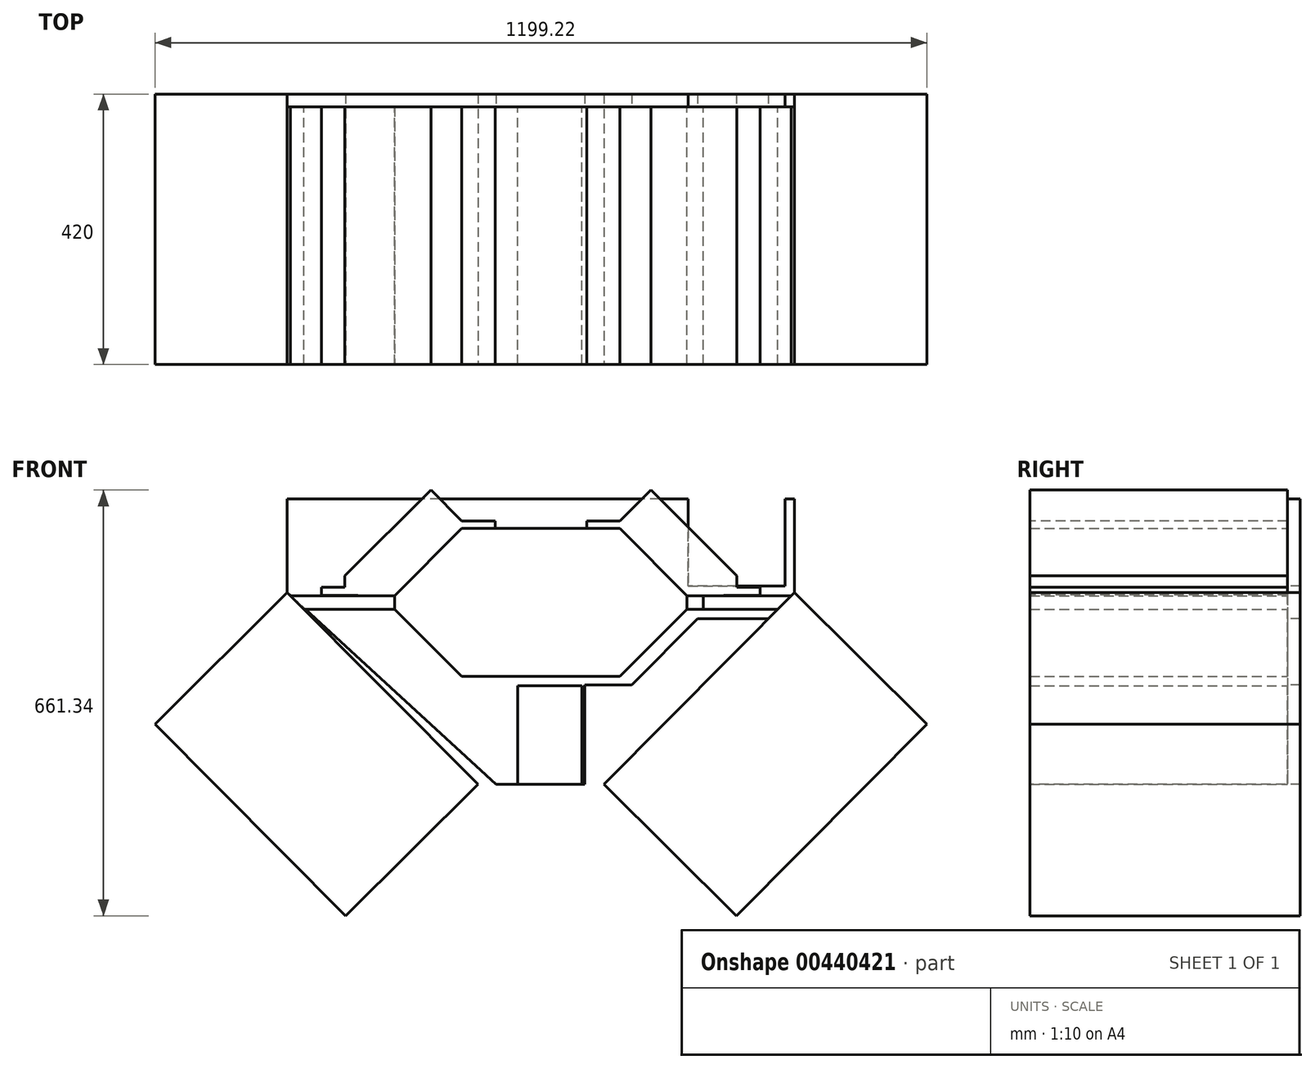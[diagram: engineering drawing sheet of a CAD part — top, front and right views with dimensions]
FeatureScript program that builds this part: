
annotation { "Feature Type Name" : "Feature", "Feature Type Description" : "" }
export const myFeature = defineFeature(function(context is Context, id is Id, definition is map)
    precondition{}
    {
        {
            var Q0;
            Q0=qCreatedBy(makeId("Front.planeOp"),FACE);
            var sketch = newSketch(context, id + "F0", { "sketchPlane" : qUnion([Q0])});
            skLineSegment(sketch, "E0", {"start": v(-123, -114.98) * mm, "end": v(-227.04, -10.5) * mm});
            skLineSegment(sketch, "E1", {"start": v(-227.04, -10.5) * mm, "end": v(-227.04, 10.5) * mm});
            skLineSegment(sketch, "E2", {"start": v(-227.04, 10.5) * mm, "end": v(-123.04, 115.02) * mm});
            skLineSegment(sketch, "E3", {"start": v(-123.04, 115.02) * mm, "end": v(122.96, 115.02) * mm});
            skLineSegment(sketch, "E4", {"start": v(122.96, 115.02) * mm, "end": v(226.96, 10.5) * mm});
            skLineSegment(sketch, "E5", {"start": v(226.96, 10.5) * mm, "end": v(226.96, -10.5) * mm});
            skLineSegment(sketch, "E6", {"start": v(226.96, -10.5) * mm, "end": v(123, -115.06) * mm});
            skLineSegment(sketch, "E7", {"start": v(123, -115.06) * mm, "end": v(-123, -114.98) * mm});
            skLineSegment(sketch, "E8", {"start": v(-106.88, 0) * mm, "end": v(-643.2, 0) * mm, "construction": true});
            skPoint(sketch, "E8.startSnap0", {"position": v(226.96, 0) * mm});
            skPoint(sketch, "E8.endSnap0", {"position": v(-227.04, 0) * mm});
            skPoint(sketch, "E9.endSnap0", {"position": v(0, -115.02) * mm});
            skLineSegment(sketch, "E10", {"start": v(0, -278.91) * mm, "end": v(0, 42.54) * mm, "construction": true});
            skPoint(sketch, "E11", {"position": v(0, 0) * mm});
            skSolve(sketch);
        }
        {
            var Q0;
            Q0=makeQuery(id+"F0.imprint","IMPRINT",FACE,{"disambiguationData":[TD([[makeQuery(id+"F0.imprint","IMPRINT",EDGE,{"derivedFrom":sQuery(id+"F0.wireOp",EDGE,"E0")}),-1.0]])]});
            extrude(context, id + "F1", {"entities" : qUnion([Q0]), "depth" : 400 * mm});
        }
        {
            var Q0;
            Q0=makeQuery(id+"F1.opExtrude","SWEPT_FACE",FACE,{"disambiguationData":[OSD([sQuery(id+"F0.wireOp",EDGE,"E5")])]});
            extrude(context, id + "F2", {"entities" : qUnion([Q0]), "depth" : 25 * mm});
        }
        {
            var Q0;
            Q0=makeQuery(id+"F1.opExtrude","CAP_FACE",FACE,{"disambiguationData":[OSD([sQuery(id+"F0.wireOp",EDGE,"E0"),sQuery(id+"F0.wireOp",EDGE,"E1"),sQuery(id+"F0.wireOp",EDGE,"E2"),sQuery(id+"F0.wireOp",EDGE,"E3"),sQuery(id+"F0.wireOp",EDGE,"E4"),sQuery(id+"F0.wireOp",EDGE,"E5"),sQuery(id+"F0.wireOp",EDGE,"E6"),sQuery(id+"F0.wireOp",EDGE,"E7")])],"isStart":false});
            var sketch = newSketch(context, id + "F3", { "sketchPlane" : qUnion([Q0])});
            skLineSegment(sketch, "E12.0", {"start": v(226.96, -10.5) * mm, "end": v(123, -115.06) * mm, "construction": true});
            skLineSegment(sketch, "E13.0", {"start": v(263.26, -115.82) * mm, "end": v(97.84, -282.21) * mm, "construction": true});
            skLineSegment(sketch, "E14.bottom", {"start": v(97.84, -282.21) * mm, "end": v(303.5, -486.67) * mm});
            skLineSegment(sketch, "E14.top", {"start": v(393.95, 15.64) * mm, "end": v(599.61, -188.82) * mm});
            skLineSegment(sketch, "E14.left", {"start": v(97.84, -282.21) * mm, "end": v(393.95, 15.64) * mm});
            skLineSegment(sketch, "E14.right", {"start": v(303.5, -486.67) * mm, "end": v(599.61, -188.82) * mm});
            skLineSegment(sketch, "E15", {"start": v(97.84, -282.21) * mm, "end": v(599.61, -188.82) * mm, "construction": true});
            skLineSegment(sketch, "E16", {"start": v(393.95, 15.64) * mm, "end": v(303.5, -486.67) * mm, "construction": true});
            skPoint(sketch, "E17", {"position": v(348.72, -235.52) * mm});
            skPoint(sketch, "E18", {"position": v(174.98, -62.78) * mm});
            skLineSegment(sketch, "E19", {"start": v(174.98, -62.78) * mm, "end": v(348.72, -235.52) * mm, "construction": true});
            skSolve(sketch);
        }
        {
            var Q0;
            Q0=makeQuery(id+"F3.imprint","IMPRINT",FACE,{"disambiguationData":[TD([[makeQuery(id+"F3.imprint","IMPRINT",EDGE,{"derivedFrom":sQuery(id+"F3.wireOp",EDGE,"E14.bottom")}),1.0]])]});
            extrude(context, id + "F4", {"entities" : qUnion([Q0]), "oppositeDirection" : true, "depth" : 420 * mm});
        }
        {
            var Q0;
            Q0=makeQuery(id+"F4.opExtrude","SWEPT_BODY",BODY,{"disambiguationData":[OSD([sQuery(id+"F3.wireOp",EDGE,"E14.bottom"),sQuery(id+"F3.wireOp",EDGE,"E14.top"),sQuery(id+"F3.wireOp",EDGE,"E14.left"),sQuery(id+"F3.wireOp",EDGE,"E14.right")])]});
            var Q1;
            Q1=qCreatedBy(makeId("Right.planeOp"),FACE);
            mirror(context, id + "F5", {"entities" : qUnion([Q0]), "mirrorPlane" : qUnion([Q1])});
        }
        {
            var Q0;
            Q0=makeQuery(id+"F2.opExtrude","CAP_FACE",FACE,{"disambiguationData":[OSD([sQuery(id+"F0.wireOp",EDGE,"E5")])],"isStart":false});
            extrude(context, id + "F6", {"entities" : qUnion([Q0]), "endBound" : BoundingType.UP_TO_NEXT, "depth" : 25 * mm});
        }
        {
            var Q0;
            Q0=makeQuery(id+"F1.opExtrude","SWEPT_FACE",FACE,{"disambiguationData":[OSD([sQuery(id+"F0.wireOp",EDGE,"E1")])]});
            extrude(context, id + "F7", {"entities" : qUnion([Q0]), "endBound" : BoundingType.UP_TO_NEXT, "depth" : 25 * mm});
        }
        {
            var Q0;
            Q0=makeQuery(id+"F1.opExtrude","CAP_FACE",FACE,{"disambiguationData":[OSD([sQuery(id+"F0.wireOp",EDGE,"E0"),sQuery(id+"F0.wireOp",EDGE,"E1"),sQuery(id+"F0.wireOp",EDGE,"E2"),sQuery(id+"F0.wireOp",EDGE,"E3"),sQuery(id+"F0.wireOp",EDGE,"E4"),sQuery(id+"F0.wireOp",EDGE,"E5"),sQuery(id+"F0.wireOp",EDGE,"E6"),sQuery(id+"F0.wireOp",EDGE,"E7")])],"isStart":false});
            var sketch = newSketch(context, id + "F8", { "sketchPlane" : qUnion([Q0])});
            skLineSegment(sketch, "E20", {"start": v(122.96, 115.02) * mm, "end": v(71.26, 115.02) * mm});
            skLineSegment(sketch, "E21", {"start": v(71.26, 115.02) * mm, "end": v(71.26, 126.66) * mm});
            skLineSegment(sketch, "E22", {"start": v(71.26, 126.66) * mm, "end": v(122.96, 126.66) * mm});
            skLineSegment(sketch, "E23", {"start": v(122.96, 126.66) * mm, "end": v(170.93, 174.67) * mm});
            skLineSegment(sketch, "E24", {"start": v(170.93, 174.67) * mm, "end": v(304.57, 41.13) * mm});
            skLineSegment(sketch, "E25", {"start": v(304.57, 41.13) * mm, "end": v(304.57, 23.86) * mm});
            skLineSegment(sketch, "E26", {"start": v(304.57, 23.86) * mm, "end": v(340.52, 23.86) * mm});
            skLineSegment(sketch, "E27", {"start": v(340.52, 23.86) * mm, "end": v(340.52, 11.86) * mm});
            skLineSegment(sketch, "E28", {"start": v(340.52, 11.86) * mm, "end": v(226.96, 10.5) * mm});
            skLineSegment(sketch, "E29", {"start": v(226.96, 10.5) * mm, "end": v(122.96, 115.02) * mm});
            skSolve(sketch);
        }
        {
            var Q0;
            Q0=makeQuery(id+"F8.imprint","IMPRINT",FACE,{"disambiguationData":[TD([[makeQuery(id+"F8.imprint","IMPRINT",EDGE,{"derivedFrom":sQuery(id+"F8.wireOp",EDGE,"E20")}),1.0]])]});
            extrude(context, id + "F9", {"entities" : qUnion([Q0]), "oppositeDirection" : true, "depth" : 400 * mm});
        }
        {
            var Q0;
            Q0=makeQuery(id+"F9.opExtrude","SWEPT_BODY",BODY,{"disambiguationData":[OSD([sQuery(id+"F8.wireOp",EDGE,"E20"),sQuery(id+"F8.wireOp",EDGE,"E21"),sQuery(id+"F8.wireOp",EDGE,"E22"),sQuery(id+"F8.wireOp",EDGE,"E23"),sQuery(id+"F8.wireOp",EDGE,"E24"),sQuery(id+"F8.wireOp",EDGE,"E25"),sQuery(id+"F8.wireOp",EDGE,"E26"),sQuery(id+"F8.wireOp",EDGE,"E27"),sQuery(id+"F8.wireOp",EDGE,"E28"),sQuery(id+"F8.wireOp",EDGE,"E29")])]});
            var Q1;
            Q1=qCreatedBy(makeId("Right.planeOp"),FACE);
            mirror(context, id + "F10", {"entities" : qUnion([Q0]), "mirrorPlane" : qUnion([Q1])});
        }
        {
            var Q0;
            Q0=makeQuery(id+"F1.opExtrude","CAP_FACE",FACE,{"disambiguationData":[OSD([sQuery(id+"F0.wireOp",EDGE,"E0"),sQuery(id+"F0.wireOp",EDGE,"E1"),sQuery(id+"F0.wireOp",EDGE,"E2"),sQuery(id+"F0.wireOp",EDGE,"E3"),sQuery(id+"F0.wireOp",EDGE,"E4"),sQuery(id+"F0.wireOp",EDGE,"E5"),sQuery(id+"F0.wireOp",EDGE,"E6"),sQuery(id+"F0.wireOp",EDGE,"E7")])],"isStart":true});
            var sketch = newSketch(context, id + "F11", { "sketchPlane" : qUnion([Q0])});
            skLineSegment(sketch, "E30", {"start": v(-226.96, -10.5) * mm, "end": v(-367.97, -10.5) * mm});
            skLineSegment(sketch, "E31", {"start": v(-367.97, -10.5) * mm, "end": v(-393.95, 15.64) * mm});
            skLineSegment(sketch, "E32", {"start": v(-393.95, 15.64) * mm, "end": v(-393.95, 160.92) * mm});
            skLineSegment(sketch, "E33", {"start": v(-393.95, 160.92) * mm, "end": v(-186.53, 160.92) * mm});
            skLineSegment(sketch, "E34", {"start": v(-186.53, 160.92) * mm, "end": v(156.41, 160.92) * mm});
            skLineSegment(sketch, "E35", {"start": v(156.41, 160.92) * mm, "end": v(393.95, 160.92) * mm});
            skLineSegment(sketch, "E36", {"start": v(393.95, 160.92) * mm, "end": v(393.95, 15.64) * mm});
            skLineSegment(sketch, "E37", {"start": v(393.95, 15.64) * mm, "end": v(69.96, -282.21) * mm});
            skLineSegment(sketch, "E38", {"start": v(69.96, -282.21) * mm, "end": v(-97.84, -282.21) * mm});
            skLineSegment(sketch, "E39", {"start": v(-97.84, -282.21) * mm, "end": v(-367.97, -10.5) * mm});
            skPoint(sketch, "E40.0", {"position": v(-393.95, 15.64) * mm});
            skPoint(sketch, "E41.0", {"position": v(-97.84, -282.21) * mm});
            skPoint(sketch, "E42.0", {"position": v(97.84, -282.21) * mm});
            skPoint(sketch, "E43.0", {"position": v(393.95, 15.64) * mm});
            skPoint(sketch, "E44.0", {"position": v(-367.97, -10.5) * mm});
            skSolve(sketch);
        }
        {
            var Q0;
            Q0=makeQuery(id+"F11.imprint","IMPRINT",FACE,{"disambiguationData":[TD([[makeQuery(id+"F11.imprint","IMPRINT",EDGE,{"derivedFrom":sQuery(id+"F11.wireOp",EDGE,"E31")}),-1.0]])]});
            var Q1;
            Q1=makeQuery(id+"F11.imprint","IMPRINT",FACE,{"disambiguationData":[TD([[makeQuery(id+"F11.imprint","IMPRINT",EDGE,{"derivedFrom":makeQuery(id+"F1.opExtrude","CAP_EDGE",EDGE,{"disambiguationData":[OSD([sQuery(id+"F0.wireOp",EDGE,"E0")])],"isStart":true})}),1.0]])]});
            extrude(context, id + "F12", {"entities" : qUnion([Q0, Q1]), "depth" : 20 * mm});
        }
        {
            var Q0;
            Q0=makeQuery(id+"F12.opExtrude","CAP_FACE",FACE,{"disambiguationData":[OSD([sQuery(id+"F11.wireOp",EDGE,"E31"),sQuery(id+"F11.wireOp",EDGE,"E32"),sQuery(id+"F11.wireOp",EDGE,"E33"),sQuery(id+"F11.wireOp",EDGE,"E34"),sQuery(id+"F11.wireOp",EDGE,"E35"),sQuery(id+"F11.wireOp",EDGE,"E36"),sQuery(id+"F11.wireOp",EDGE,"E37"),sQuery(id+"F11.wireOp",EDGE,"E38"),sQuery(id+"F11.wireOp",EDGE,"E39")])],"isStart":true});
            var sketch = newSketch(context, id + "F13", { "sketchPlane" : qUnion([Q0])});
            skLineSegment(sketch, "E45", {"start": v(353.05, -25.5) * mm, "end": v(243.07, -25.5) * mm});
            skLineSegment(sketch, "E46", {"start": v(243.07, -25.5) * mm, "end": v(140.84, -128.33) * mm});
            skLineSegment(sketch, "E47", {"start": v(67.84, -128.33) * mm, "end": v(67.84, -282.21) * mm});
            skLineSegment(sketch, "E48", {"start": v(67.84, -282.21) * mm, "end": v(97.84, -282.21) * mm});
            skLineSegment(sketch, "E49", {"start": v(97.84, -282.21) * mm, "end": v(353.05, -25.5) * mm});
            skLineSegment(sketch, "E50.bottom", {"start": v(378.95, 25.5) * mm, "end": v(228.95, 25.5) * mm});
            skLineSegment(sketch, "E50.top", {"start": v(378.95, 165.5) * mm, "end": v(228.95, 165.5) * mm});
            skLineSegment(sketch, "E50.left", {"start": v(378.95, 25.5) * mm, "end": v(378.95, 165.5) * mm});
            skLineSegment(sketch, "E50.right", {"start": v(228.95, 25.5) * mm, "end": v(228.95, 165.5) * mm});
            skLineSegment(sketch, "E51.MirrorCS", {"start": v(-228.95, 25.5) * mm, "end": v(-228.95, 165.5) * mm});
            skLineSegment(sketch, "E52.MirrorCS", {"start": v(-378.95, 165.5) * mm, "end": v(-228.95, 165.5) * mm});
            skLineSegment(sketch, "E53.MirrorCS", {"start": v(-378.95, 25.5) * mm, "end": v(-378.95, 165.5) * mm});
            skLineSegment(sketch, "E54.MirrorCS", {"start": v(-378.95, 25.5) * mm, "end": v(-228.95, 25.5) * mm});
            skLineSegment(sketch, "E55.MirrorCS", {"start": v(-353.05, -25.5) * mm, "end": v(-243.07, -25.5) * mm});
            skLineSegment(sketch, "E56.MirrorCS", {"start": v(-97.84, -282.21) * mm, "end": v(-353.05, -25.5) * mm});
            skLineSegment(sketch, "E57.MirrorCS", {"start": v(-67.84, -282.21) * mm, "end": v(-97.84, -282.21) * mm});
            skLineSegment(sketch, "E58", {"start": v(140.84, -128.33) * mm, "end": v(67.84, -128.33) * mm});
            skLineSegment(sketch, "E59.MirrorCS", {"start": v(-67.84, -128.33) * mm, "end": v(-67.84, -282.21) * mm});
            skLineSegment(sketch, "E60.MirrorCS", {"start": v(-140.84, -128.33) * mm, "end": v(-67.84, -128.33) * mm});
            skLineSegment(sketch, "E61.MirrorCS", {"start": v(-243.07, -25.5) * mm, "end": v(-140.84, -128.33) * mm});
            skLineSegment(sketch, "E62.bottom", {"start": v(13.94, -282.21) * mm, "end": v(-36.06, -282.21) * mm});
            skLineSegment(sketch, "E62.top", {"start": v(13.94, -129.54) * mm, "end": v(-36.06, -129.54) * mm});
            skLineSegment(sketch, "E62.left", {"start": v(13.94, -282.21) * mm, "end": v(13.94, -129.54) * mm, "construction": true});
            skLineSegment(sketch, "E62.right", {"start": v(-36.06, -282.21) * mm, "end": v(-36.06, -129.54) * mm});
            skLineSegment(sketch, "E63.MirrorCS", {"start": v(13.94, -129.54) * mm, "end": v(63.94, -129.54) * mm});
            skLineSegment(sketch, "E64.MirrorCS", {"start": v(63.94, -282.21) * mm, "end": v(63.94, -129.54) * mm});
            skLineSegment(sketch, "E65.MirrorCS", {"start": v(13.94, -282.21) * mm, "end": v(63.94, -282.21) * mm});
            skSolve(sketch);
        }
        {
            var Q0;
            Q0=makeQuery(id+"F13.imprint","IMPRINT",FACE,{"disambiguationData":[TD([[makeQuery(id+"F13.imprint","IMPRINT",EDGE,{"derivedFrom":sQuery(id+"F13.wireOp",EDGE,"E62.bottom")}),1.0]])]});
            extrude(context, id + "F14", {"entities" : qUnion([Q0]), "depth" : 400 * mm});
        }
        {
            var Q0;
            Q0=makeQuery(id+"F13.imprint","IMPRINT",FACE,{"disambiguationData":[TD([[makeQuery(id+"F13.imprint","IMPRINT",EDGE,{"derivedFrom":sQuery(id+"F13.wireOp",EDGE,"E55.MirrorCS")}),-1.0]])]});
            var Q1;
            Q1=makeQuery(id+"F13.imprint","IMPRINT",FACE,{"disambiguationData":[TD([[makeQuery(id+"F13.imprint","IMPRINT",EDGE,{"derivedFrom":sQuery(id+"F13.wireOp",EDGE,"E45")}),1.0]])]});
            var Q2;
            Q2=makeQuery(id+"F13.imprint","IMPRINT",FACE,{"disambiguationData":[TD([[makeQuery(id+"F13.imprint","IMPRINT",EDGE,{"derivedFrom":sQuery(id+"F13.wireOp",EDGE,"E50.bottom")}),-1.0]])]});
            var Q3;
            Q3=makeQuery(id+"F13.imprint","IMPRINT",FACE,{"disambiguationData":[TD([[makeQuery(id+"F13.imprint","IMPRINT",EDGE,{"derivedFrom":sQuery(id+"F13.wireOp",EDGE,"E52.MirrorCS")}),-1.0]])]});
            extrude(context, id + "F15", {"entities" : qUnion([Q0, Q1, Q2, Q3]), "operationType" : NewBodyOperationType.REMOVE, "oppositeDirection" : true, "depth" : 25 * mm});
        }
    });
